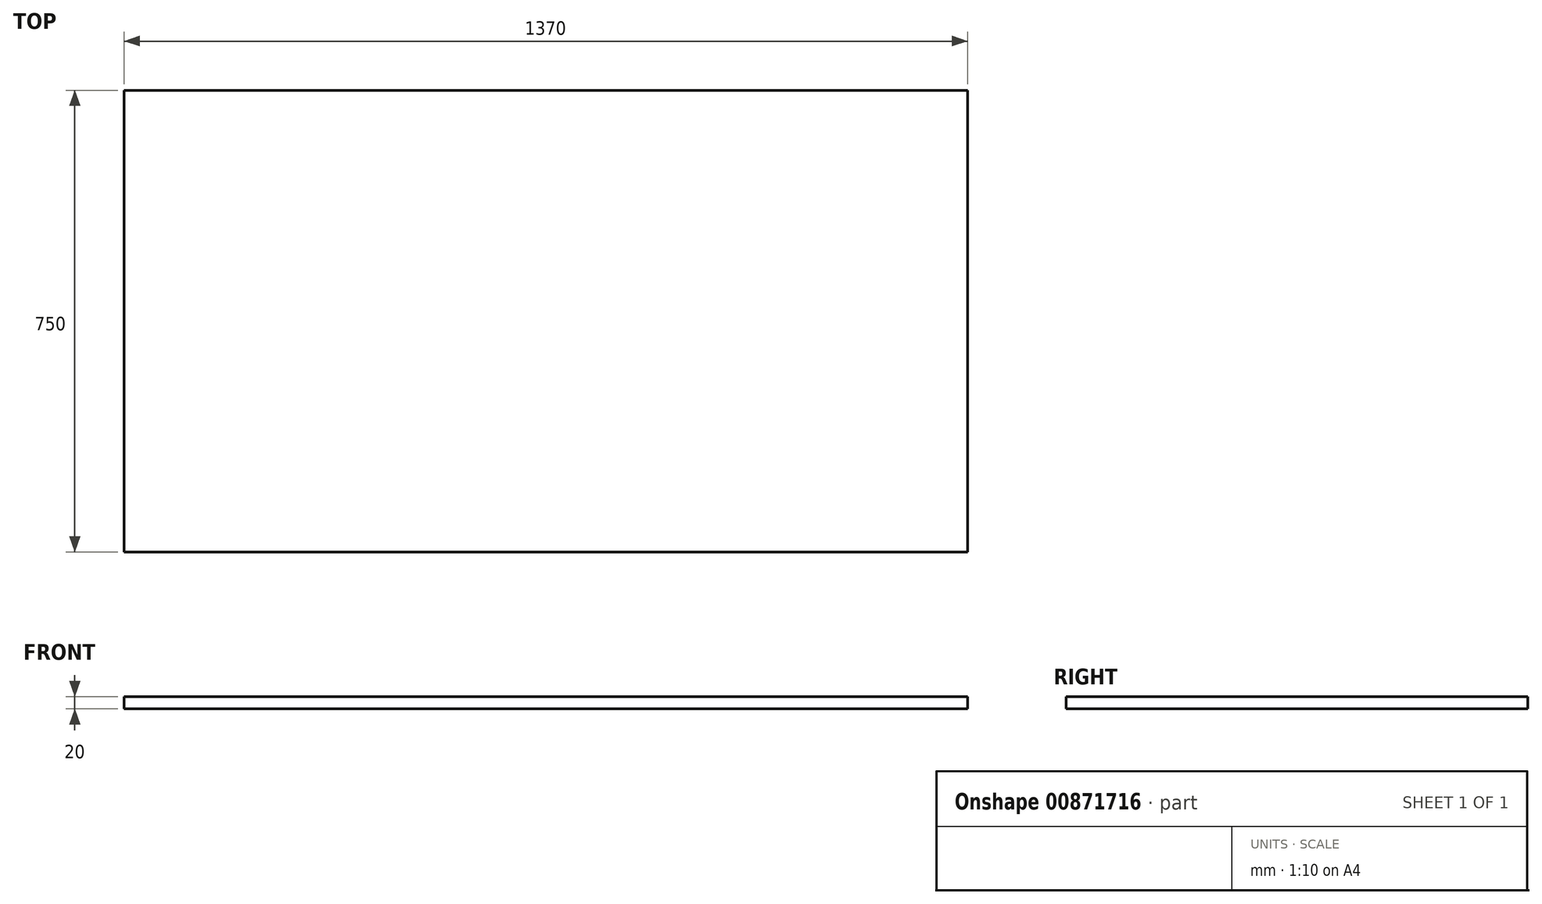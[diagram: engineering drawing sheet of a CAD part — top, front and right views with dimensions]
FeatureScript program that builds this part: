
annotation { "Feature Type Name" : "Feature", "Feature Type Description" : "" }
export const myFeature = defineFeature(function(context is Context, id is Id, definition is map)
    precondition{}
    {
        {
            var Q0;
            Q0=qCreatedBy(makeId("Top.planeOp"),FACE);
            var sketch = newSketch(context, id + "F0", { "sketchPlane" : qUnion([Q0])});
            skLineSegment(sketch, "E0.bottom", {"start": v(0, 0) * mm, "end": v(1370, 0) * mm});
            skLineSegment(sketch, "E0.top", {"start": v(0, 750) * mm, "end": v(1370, 750) * mm});
            skLineSegment(sketch, "E0.left", {"start": v(0, 0) * mm, "end": v(0, 750) * mm});
            skLineSegment(sketch, "E0.right", {"start": v(1370, 0) * mm, "end": v(1370, 750) * mm});
            skSolve(sketch);
        }
        {
            var Q0;
            Q0 = qSketchRegion(id + "F0", true);
            extrude(context, id + "F1", {"entities" : qUnion([Q0]), "depth" : 20 * mm, "offsetDistance" : 25 * mm});
        }
    });
